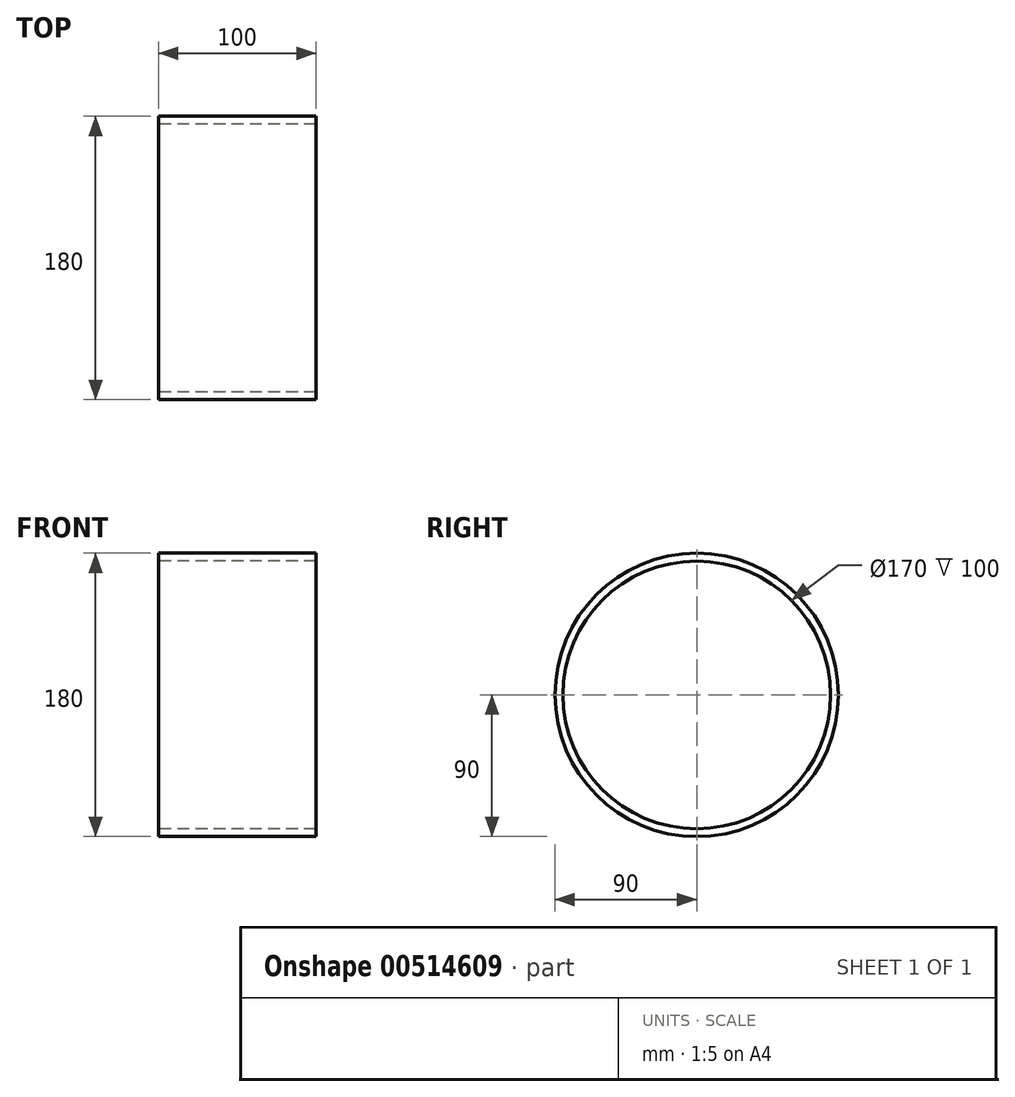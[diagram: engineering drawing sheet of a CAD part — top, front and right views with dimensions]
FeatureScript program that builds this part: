
annotation { "Feature Type Name" : "Feature", "Feature Type Description" : "" }
export const myFeature = defineFeature(function(context is Context, id is Id, definition is map)
    precondition{}
    {
        {
            var Q0;
            Q0=qCreatedBy(makeId("Front.planeOp"),FACE);
            var sketch = newSketch(context, id + "F0", { "sketchPlane" : qUnion([Q0])});
            skLineSegment(sketch, "E0", {"start": v(-84.83, 0) * mm, "end": v(92.67, 0) * mm, "construction": true});
            skLineSegment(sketch, "E1", {"start": v(0, 90) * mm, "end": v(100, 90) * mm});
            skLineSegment(sketch, "E2", {"start": v(100, 90) * mm, "end": v(100, 85) * mm});
            skLineSegment(sketch, "E3", {"start": v(100, 85) * mm, "end": v(0, 85) * mm});
            skLineSegment(sketch, "E4", {"start": v(0, 85) * mm, "end": v(0, 90) * mm});
            skSolve(sketch);
        }
        {
            var Q0;
            Q0 = qSketchRegion(id + "F0", true);
            var Q1;
            Q1=sQuery(id+"F0.wireOp",EDGE,"E0");
            revolve(context, id + "F1", {"entities" : qUnion([Q0]), "axis" : qUnion([Q1]), "revolveType" : RevolveType.FULL});
        }
    });
